# Revit family: LRTJ1x1_1x4
name_source: partatom
category: Lighting Fixtures
units: mm (PartAtom-declared; Revit-internal decimal feet)

## family parameters
Always vertical = Yes
Cut with Voids When Loaded = No
Host = Ceiling
Light Source = Yes
OmniClass Number = 23.80.70.11.14.17
OmniClass Title = Direct/Indirect
Part Type = Normal
Room Calculation Point = No
Round Connector Dimension = Use Diameter
Shared = No

## types (3) — shared parameters
Assembly Code = D5020200
Color Filter = 16777215
Description = LED Troffer Dish High-Efficiency
Dimming Lamp Color Temperature Shift = <None>
Emit Shape Visible in Rendering = No
Emit from Rectangle Width = 0' - 11 3/4"
Housing Finish = Metal - Viscor - White
Lamp = LED
Lens Finish = Acrylic - Viscor - Frosted Round Linear Ribbed
Manufacturer = VISIONEERING by VISCOR
Model = LRTJ
Tilt Angle = 90.00°
URL = https://www.viscor.com
Voltage = 120 V
Width = 0' - 11 3/4"

## per-type parameters (varying)
| type | Apparent Load | Emit from Rectangle Length | Lamp Wattage | Length | Photometric Web File |
| LRTJ1X1-LED840K016LUNV | 15 VA | 0' - 11 3/4" | 15 VA | 0' - 11 3/4" | LRTJ1x1-LED840K016LUNV.ies |
| LRTJ1x4-LED840K020LUNV | 17 VA | 3' - 11 3/4" | 17 VA | 3' - 11 3/4" | LRTJ1x4-LED840K020LUNV-G001846.IES |
| LRTJ1x4-LED840K033LUNV | 26 VA | 3' - 11 3/4" | 26 VA | 3' - 11 3/4" | LRTJ1x4-LED840K033LUNV-G001840.IES |

## geometry (parser evidence)
native form markers: Sweep x3
no freeform markers — native parametric forms only
